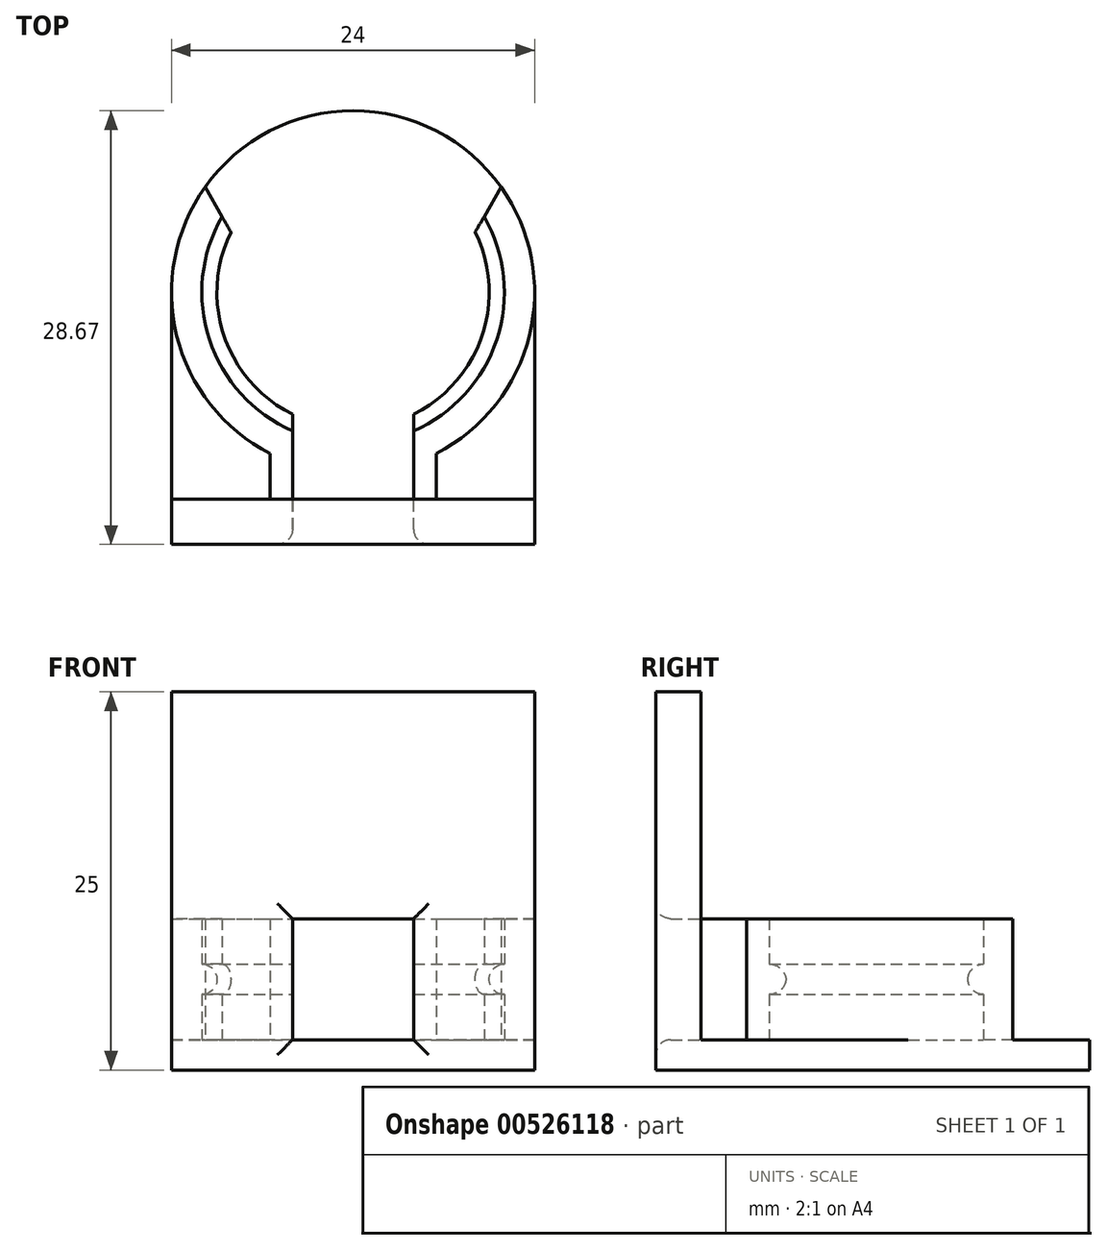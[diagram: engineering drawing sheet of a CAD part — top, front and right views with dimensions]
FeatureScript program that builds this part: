
annotation { "Feature Type Name" : "Feature", "Feature Type Description" : "" }
export const myFeature = defineFeature(function(context is Context, id is Id, definition is map)
    precondition{}
    {
        {
            var Q0;
            Q0=qCreatedBy(makeId("Top.planeOp"),FACE);
            var sketch = newSketch(context, id + "F0", { "sketchPlane" : qUnion([Q0])});
            skArc(sketch, "E0", {"start": v(-5.5, 1.5) * mm, "mid": v(0, 24.17) * mm, "end": v(5.5, 1.5) * mm});
            skArc(sketch, "E1", {"start": v(-5.5, -1.5) * mm, "mid": v(0, -24.17) * mm, "end": v(5.5, -1.5) * mm});
            skLineSegment(sketch, "E2", {"start": v(-5.5, 1.5) * mm, "end": v(-5.5, -1.5) * mm});
            skLineSegment(sketch, "E3", {"start": v(5.5, 1.5) * mm, "end": v(5.5, -1.5) * mm});
            skSolve(sketch);
        }
        {
            var Q0;
            Q0=qSketchRegion(id+"F0",true);
            extrude(context, id + "F1", {"entities" : qUnion([Q0]), "depth" : 2 * mm, "offsetDistance" : 25 * mm});
        }
        {
            var Q0;
            Q0=makeQuery(id+"F1.opExtrude","CAP_FACE",FACE,{"disambiguationData":[OSD([sQuery(id+"F0.wireOp",EDGE,"E0"),sQuery(id+"F0.wireOp",EDGE,"E1"),sQuery(id+"F0.wireOp",EDGE,"E2"),sQuery(id+"F0.wireOp",EDGE,"E3")])],"isStart":false});
            var sketch = newSketch(context, id + "F2", { "sketchPlane" : qUnion([Q0])});
            skArc(sketch, "E4", {"start": v(8.66, 17.17) * mm, "mid": v(9.5, 9.04) * mm, "end": v(4, 3) * mm});
            skArc(sketch, "E5", {"start": v(9.78, 19.11) * mm, "mid": v(11.66, 9.33) * mm, "end": v(5.5, 1.5) * mm});
            skArc(sketch, "E6", {"start": v(-8.66, 17.17) * mm, "mid": v(-9.5, 9.04) * mm, "end": v(-4, 3) * mm});
            skArc(sketch, "E7", {"start": v(5.5, -3.81) * mm, "mid": v(9.59, -9.32) * mm, "end": v(9.17, -16.17) * mm});
            skLineSegment(sketch, "E8", {"start": v(9.78, 19.11) * mm, "end": v(8.66, 17.17) * mm});
            skLineSegment(sketch, "E9", {"start": v(-8.66, 17.17) * mm, "end": v(-9.78, 19.11) * mm});
            skLineSegment(sketch, "E10", {"start": v(5.5, 1.5) * mm, "end": v(5.5, -3.81) * mm});
            skLineSegment(sketch, "E11", {"start": v(-4, 3) * mm, "end": v(-4, -6.24) * mm});
            skLineSegment(sketch, "E12", {"start": v(-4, -6.24) * mm, "end": v(-9.17, -16.17) * mm});
            skLineSegment(sketch, "E13", {"start": v(9.17, -16.17) * mm, "end": v(4, -6.24) * mm});
            skLineSegment(sketch, "E14", {"start": v(4, -6.24) * mm, "end": v(4, 3) * mm});
            skArc(sketch, "E15", {"start": v(-9.78, 19.11) * mm, "mid": v(-11.66, 9.33) * mm, "end": v(-5.5, 1.5) * mm});
            skArc(sketch, "E16", {"start": v(-9.17, -16.17) * mm, "mid": v(-9.59, -9.32) * mm, "end": v(-5.5, -3.81) * mm});
            skLineSegment(sketch, "E17", {"start": v(-5.5, 1.5) * mm, "end": v(-5.5, -3.81) * mm});
            skArc(sketch, "E18.0", {"start": v(-5.5, 1.5) * mm, "mid": v(0, 24.17) * mm, "end": v(5.5, 1.5) * mm, "construction": true});
            skArc(sketch, "E19.0", {"start": v(-5.5, -1.5) * mm, "mid": v(0, -24.17) * mm, "end": v(5.5, -1.5) * mm, "construction": true});
            skSolve(sketch);
        }
        {
            var Q0;
            Q0=qSketchRegion(id+"F2",true);
            extrude(context, id + "F3", {"entities" : qUnion([Q0]), "operationType" : NewBodyOperationType.ADD, "depth" : 3 * mm, "offsetDistance" : 25 * mm});
        }
        {
            var Q0;
            Q0=makeQuery(id+"F3.opExtrude","CAP_FACE",FACE,{"disambiguationData":[OSD([sQuery(id+"F2.wireOp",EDGE,"E4"),sQuery(id+"F2.wireOp",EDGE,"E5"),sQuery(id+"F2.wireOp",EDGE,"E7"),sQuery(id+"F2.wireOp",EDGE,"E8"),sQuery(id+"F2.wireOp",EDGE,"E10"),sQuery(id+"F2.wireOp",EDGE,"E13"),sQuery(id+"F2.wireOp",EDGE,"E14")])],"isStart":false});
            var sketch = newSketch(context, id + "F4", { "sketchPlane" : qUnion([Q0])});
            skArc(sketch, "E20", {"start": v(-9.78, 19.11) * mm, "mid": v(-11.66, 9.33) * mm, "end": v(-5.5, 1.5) * mm});
            skArc(sketch, "E21", {"start": v(9.78, 19.11) * mm, "mid": v(11.66, 9.33) * mm, "end": v(5.5, 1.5) * mm});
            skArc(sketch, "E22", {"start": v(8.07, 16.15) * mm, "mid": v(8.53, 9.28) * mm, "end": v(4, 4.1) * mm});
            skArc(sketch, "E23", {"start": v(-8.07, 16.15) * mm, "mid": v(-8.53, 9.28) * mm, "end": v(-4, 4.1) * mm});
            skArc(sketch, "E24", {"start": v(5.5, -5.04) * mm, "mid": v(8.6, -9.53) * mm, "end": v(8.55, -14.98) * mm});
            skArc(sketch, "E25", {"start": v(-5.5, -5.04) * mm, "mid": v(-8.6, -9.53) * mm, "end": v(-8.55, -14.98) * mm});
            skLineSegment(sketch, "E26", {"start": v(-5.5, 1.5) * mm, "end": v(-5.5, -5.04) * mm});
            skLineSegment(sketch, "E27", {"start": v(5.5, 1.5) * mm, "end": v(5.5, -5.04) * mm});
            skLineSegment(sketch, "E28", {"start": v(-4, 4.1) * mm, "end": v(-4, -6.24) * mm});
            skLineSegment(sketch, "E29", {"start": v(-4, -6.24) * mm, "end": v(-8.55, -14.98) * mm});
            skLineSegment(sketch, "E30", {"start": v(4, 4.1) * mm, "end": v(4, -6.24) * mm});
            skLineSegment(sketch, "E31", {"start": v(4, -6.24) * mm, "end": v(8.55, -14.98) * mm});
            skLineSegment(sketch, "E32", {"start": v(8.07, 16.15) * mm, "end": v(9.78, 19.11) * mm});
            skLineSegment(sketch, "E33", {"start": v(-9.78, 19.11) * mm, "end": v(-8.07, 16.15) * mm});
            skLineSegment(sketch, "E34.0", {"start": v(-8.66, 17.17) * mm, "end": v(-9.78, 19.11) * mm, "construction": true});
            skLineSegment(sketch, "E35.0", {"start": v(9.78, 19.11) * mm, "end": v(8.66, 17.17) * mm, "construction": true});
            skLineSegment(sketch, "E36.0", {"start": v(-4, -6.24) * mm, "end": v(-9.17, -16.17) * mm, "construction": true});
            skLineSegment(sketch, "E37.0", {"start": v(9.17, -16.17) * mm, "end": v(4, -6.24) * mm, "construction": true});
            skArc(sketch, "E38.0", {"start": v(-9.78, 19.11) * mm, "mid": v(0, 24.17) * mm, "end": v(9.78, 19.11) * mm, "construction": true});
            skArc(sketch, "E39.0", {"start": v(-5.5, -1.5) * mm, "mid": v(0, -24.17) * mm, "end": v(5.5, -1.5) * mm, "construction": true});
            skSolve(sketch);
        }
        {
            var Q0;
            Q0=qSketchRegion(id+"F4",true);
            extrude(context, id + "F5", {"entities" : qUnion([Q0]), "operationType" : NewBodyOperationType.ADD, "depth" : 2 * mm, "offsetDistance" : 25 * mm});
        }
        {
            var Q0;
            Q0=makeQuery(id+"F5.opExtrude","CAP_FACE",FACE,{"disambiguationData":[OSD([sQuery(id+"F4.wireOp",EDGE,"E21"),sQuery(id+"F4.wireOp",EDGE,"E22"),sQuery(id+"F4.wireOp",EDGE,"E24"),sQuery(id+"F4.wireOp",EDGE,"E27"),sQuery(id+"F4.wireOp",EDGE,"E30"),sQuery(id+"F4.wireOp",EDGE,"E31"),sQuery(id+"F4.wireOp",EDGE,"E32")])],"isStart":false});
            var sketch = newSketch(context, id + "F6", { "sketchPlane" : qUnion([Q0])});
            skArc(sketch, "E40", {"start": v(8.66, 17.17) * mm, "mid": v(9.5, 9.04) * mm, "end": v(4, 3) * mm});
            skArc(sketch, "E41", {"start": v(9.78, 19.11) * mm, "mid": v(11.66, 9.33) * mm, "end": v(5.5, 1.5) * mm});
            skArc(sketch, "E42", {"start": v(-8.66, 17.17) * mm, "mid": v(-9.5, 9.04) * mm, "end": v(-4, 3) * mm});
            skArc(sketch, "E43", {"start": v(5.5, -3.81) * mm, "mid": v(9.59, -9.32) * mm, "end": v(9.17, -16.17) * mm});
            skLineSegment(sketch, "E44", {"start": v(9.78, 19.11) * mm, "end": v(8.66, 17.17) * mm});
            skLineSegment(sketch, "E45", {"start": v(-8.66, 17.17) * mm, "end": v(-9.78, 19.11) * mm});
            skLineSegment(sketch, "E46", {"start": v(5.5, 1.5) * mm, "end": v(5.5, -3.81) * mm});
            skLineSegment(sketch, "E47", {"start": v(-4, 3) * mm, "end": v(-4, -6.24) * mm});
            skLineSegment(sketch, "E48", {"start": v(-4, -6.24) * mm, "end": v(-9.17, -16.17) * mm});
            skLineSegment(sketch, "E49", {"start": v(9.17, -16.17) * mm, "end": v(4, -6.24) * mm});
            skLineSegment(sketch, "E50", {"start": v(4, -6.24) * mm, "end": v(4, 3) * mm});
            skArc(sketch, "E51", {"start": v(-9.78, 19.11) * mm, "mid": v(-11.66, 9.33) * mm, "end": v(-5.5, 1.5) * mm});
            skArc(sketch, "E52", {"start": v(-9.17, -16.17) * mm, "mid": v(-9.59, -9.32) * mm, "end": v(-5.5, -3.81) * mm});
            skLineSegment(sketch, "E53", {"start": v(-5.5, 1.5) * mm, "end": v(-5.5, -3.81) * mm});
            skArc(sketch, "E54.0", {"start": v(-5.5, -1.5) * mm, "mid": v(0, -24.17) * mm, "end": v(5.5, -1.5) * mm, "construction": true});
            skArc(sketch, "E55.0", {"start": v(-9.78, 19.11) * mm, "mid": v(0, 24.17) * mm, "end": v(9.78, 19.11) * mm, "construction": true});
            skSolve(sketch);
        }
        {
            var Q0;
            Q0=qSketchRegion(id+"F6",true);
            extrude(context, id + "F7", {"entities" : qUnion([Q0]), "operationType" : NewBodyOperationType.ADD, "depth" : 3 * mm, "offsetDistance" : 25 * mm});
        }
        {
            var Q0;
            Q0=makeQuery(id+"F5.opExtrude","CAP_EDGE",EDGE,{"disambiguationData":[OSD([sQuery(id+"F4.wireOp",EDGE,"E22")])],"isStart":false});
            var Q1;
            Q1=makeQuery(id+"F5.opExtrude","CAP_EDGE",EDGE,{"disambiguationData":[OSD([sQuery(id+"F4.wireOp",EDGE,"E23")])],"isStart":false});
            var Q2;
            Q2=makeQuery(id+"F5.opExtrude","CAP_EDGE",EDGE,{"disambiguationData":[OSD([sQuery(id+"F4.wireOp",EDGE,"E23")])],"isStart":true});
            var Q3;
            Q3=makeQuery(id+"F5.opExtrude","CAP_EDGE",EDGE,{"disambiguationData":[OSD([sQuery(id+"F4.wireOp",EDGE,"E22")])],"isStart":true});
            var Q4;
            Q4=makeQuery(id+"F5.opExtrude","CAP_EDGE",EDGE,{"disambiguationData":[OSD([sQuery(id+"F4.wireOp",EDGE,"E25")])],"isStart":true});
            var Q5;
            Q5=makeQuery(id+"F5.opExtrude","CAP_EDGE",EDGE,{"disambiguationData":[OSD([sQuery(id+"F4.wireOp",EDGE,"E25")])],"isStart":false});
            var Q6;
            Q6=makeQuery(id+"F5.opExtrude","CAP_EDGE",EDGE,{"disambiguationData":[OSD([sQuery(id+"F4.wireOp",EDGE,"E24")])],"isStart":false});
            var Q7;
            Q7=makeQuery(id+"F5.opExtrude","CAP_EDGE",EDGE,{"disambiguationData":[OSD([sQuery(id+"F4.wireOp",EDGE,"E24")])],"isStart":true});
            fillet(context, id + "F8", {"entities" : qUnion([Q0, Q1, Q2, Q3, Q4, Q5, Q6, Q7]), "radius" : 1 * mm, "tangentPropagation" : true, "allowEdgeOverflow" : false});
        }
        {
            var Q0;
            Q0=makeQuery(id+"F7.opExtrude","CAP_FACE",FACE,{"disambiguationData":[OSD([sQuery(id+"F6.wireOp",EDGE,"E40"),sQuery(id+"F6.wireOp",EDGE,"E41"),sQuery(id+"F6.wireOp",EDGE,"E43"),sQuery(id+"F6.wireOp",EDGE,"E44"),sQuery(id+"F6.wireOp",EDGE,"E46"),sQuery(id+"F6.wireOp",EDGE,"E49"),sQuery(id+"F6.wireOp",EDGE,"E50")])],"isStart":false});
            var sketch = newSketch(context, id + "F9", { "sketchPlane" : qUnion([Q0])});
            skLineSegment(sketch, "E56.bottom", {"start": v(-12, -1.5) * mm, "end": v(12, -1.5) * mm});
            skLineSegment(sketch, "E56.top", {"start": v(-12, -24.17) * mm, "end": v(12, -24.17) * mm});
            skLineSegment(sketch, "E56.left", {"start": v(-12, -1.5) * mm, "end": v(-12, -24.17) * mm});
            skLineSegment(sketch, "E56.right", {"start": v(12, -1.5) * mm, "end": v(12, -24.17) * mm});
            skSolve(sketch);
        }
        {
            var Q0;
            Q0=qSketchRegion(id+"F9",true);
            extrude(context, id + "F10", {"entities" : qUnion([Q0]), "operationType" : NewBodyOperationType.REMOVE, "oppositeDirection" : true, "depth" : 10 * mm, "offsetDistance" : 25 * mm});
        }
        {
            var Q0;
            Q0=makeQuery(id+"F10.boolean.opBoolean","COPY",FACE,{"derivedFrom":makeQuery(id+"F10.opExtrude","SWEPT_FACE",FACE,{"disambiguationData":[OSD([sQuery(id+"F9.wireOp",EDGE,"E56.bottom")])]})});
            var sketch = newSketch(context, id + "F11", { "sketchPlane" : qUnion([Q0])});
            skLineSegment(sketch, "E57.bottom", {"start": v(-12, 25) * mm, "end": v(12, 25) * mm});
            skLineSegment(sketch, "E57.top", {"start": v(-12, 0) * mm, "end": v(12, 0) * mm});
            skLineSegment(sketch, "E57.left", {"start": v(-12, 25) * mm, "end": v(-12, 0) * mm});
            skLineSegment(sketch, "E57.right", {"start": v(12, 25) * mm, "end": v(12, 0) * mm});
            skLineSegment(sketch, "E58.bottom", {"start": v(-4, 10) * mm, "end": v(4, 10) * mm});
            skLineSegment(sketch, "E58.top", {"start": v(-4, 2) * mm, "end": v(4, 2) * mm});
            skLineSegment(sketch, "E58.left", {"start": v(-4, 10) * mm, "end": v(-4, 2) * mm});
            skLineSegment(sketch, "E58.right", {"start": v(4, 10) * mm, "end": v(4, 2) * mm});
            skSolve(sketch);
        }
        {
            var Q0;
            Q0 = qSketchRegion(id + "F11", true);
            extrude(context, id + "F12", {"entities" : qUnion([Q0]), "operationType" : NewBodyOperationType.ADD, "depth" : 3 * mm, "offsetDistance" : 25 * mm});
        }
        {
            var Q0;
            Q0=makeQuery(id+"F12.opExtrude","CAP_EDGE",EDGE,{"disambiguationData":[OSD([sQuery(id+"F11.wireOp",EDGE,"E58.bottom")])],"isStart":false});
            var Q1;
            Q1=makeQuery(id+"F12.opExtrude","CAP_EDGE",EDGE,{"disambiguationData":[OSD([sQuery(id+"F11.wireOp",EDGE,"E58.right")])],"isStart":false});
            var Q2;
            Q2=makeQuery(id+"F12.opExtrude","CAP_EDGE",EDGE,{"disambiguationData":[OSD([sQuery(id+"F11.wireOp",EDGE,"E58.top")])],"isStart":false});
            var Q3;
            Q3=makeQuery(id+"F12.opExtrude","CAP_EDGE",EDGE,{"disambiguationData":[OSD([sQuery(id+"F11.wireOp",EDGE,"E58.left")])],"isStart":false});
            fillet(context, id + "F13", {"entities" : qUnion([Q0, Q1, Q2, Q3]), "radius" : 1 * mm, "tangentPropagation" : true, "allowEdgeOverflow" : false});
        }
        {
            var Q0;
            Q0=makeQuery(id+"F12.boolean.opBoolean","MERGE",FACE,{"derivedFrom":[makeQuery(id+"F1.opExtrude","CAP_FACE",FACE,{"disambiguationData":[OSD([sQuery(id+"F0.wireOp",EDGE,"E0"),sQuery(id+"F0.wireOp",EDGE,"E1"),sQuery(id+"F0.wireOp",EDGE,"E2"),sQuery(id+"F0.wireOp",EDGE,"E3")])],"isStart":true}),makeQuery(id+"F12.opExtrude","SWEPT_FACE",FACE,{"disambiguationData":[OSD([sQuery(id+"F11.wireOp",EDGE,"E57.top")])]})]});
            var sketch = newSketch(context, id + "F14", { "sketchPlane" : qUnion([Q0])});
            skLineSegment(sketch, "E59.bottom", {"start": v(-12, 1.5) * mm, "end": v(12, 1.5) * mm});
            skLineSegment(sketch, "E59.top", {"start": v(-12, -12.17) * mm, "end": v(12, -12.17) * mm});
            skLineSegment(sketch, "E59.left", {"start": v(-12, 1.5) * mm, "end": v(-12, -12.17) * mm});
            skLineSegment(sketch, "E59.right", {"start": v(12, 1.5) * mm, "end": v(12, -12.17) * mm});
            skSolve(sketch);
        }
        {
            var Q0;
            Q0 = qSketchRegion(id + "F14", true);
            extrude(context, id + "F15", {"entities" : qUnion([Q0]), "operationType" : NewBodyOperationType.ADD, "oppositeDirection" : true, "depth" : 2 * mm, "offsetDistance" : 25 * mm});
        }
    });
